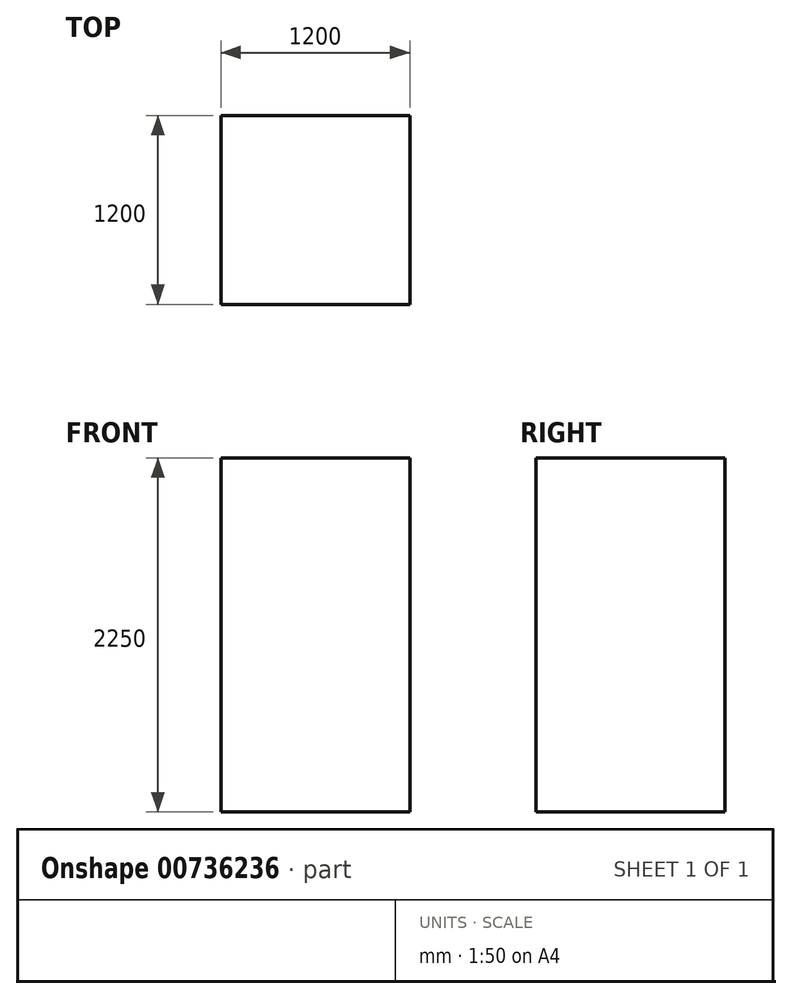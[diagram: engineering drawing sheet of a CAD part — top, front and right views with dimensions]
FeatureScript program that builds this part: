
annotation { "Feature Type Name" : "Feature", "Feature Type Description" : "" }
export const myFeature = defineFeature(function(context is Context, id is Id, definition is map)
    precondition{}
    {
        {
            var Q0;
            Q0=qCreatedBy(makeId("Front.planeOp"),FACE);
            var sketch = newSketch(context, id + "F0", { "sketchPlane" : qUnion([Q0])});
            skLineSegment(sketch, "E0.bottom", {"start": v(-598.75, 0) * mm, "end": v(601.25, 0) * mm});
            skLineSegment(sketch, "E0.top", {"start": v(-598.75, 2250) * mm, "end": v(601.25, 2250) * mm});
            skLineSegment(sketch, "E0.left", {"start": v(-598.75, 0) * mm, "end": v(-598.75, 2250) * mm});
            skLineSegment(sketch, "E0.right", {"start": v(601.25, 0) * mm, "end": v(601.25, 2250) * mm});
            skSolve(sketch);
        }
        {
            var Q0;
            Q0=makeQuery(id+"F0.imprint","IMPRINT",FACE,{"disambiguationData":[TD([[makeQuery(id+"F0.imprint","IMPRINT",EDGE,{"derivedFrom":sQuery(id+"F0.wireOp",EDGE,"E0.bottom")}),1.0]])]});
            extrude(context, id + "F1", {"entities" : qUnion([Q0]), "oppositeDirection" : true, "depth" : 1200 * mm, "offsetDistance" : 25 * mm});
        }
    });
